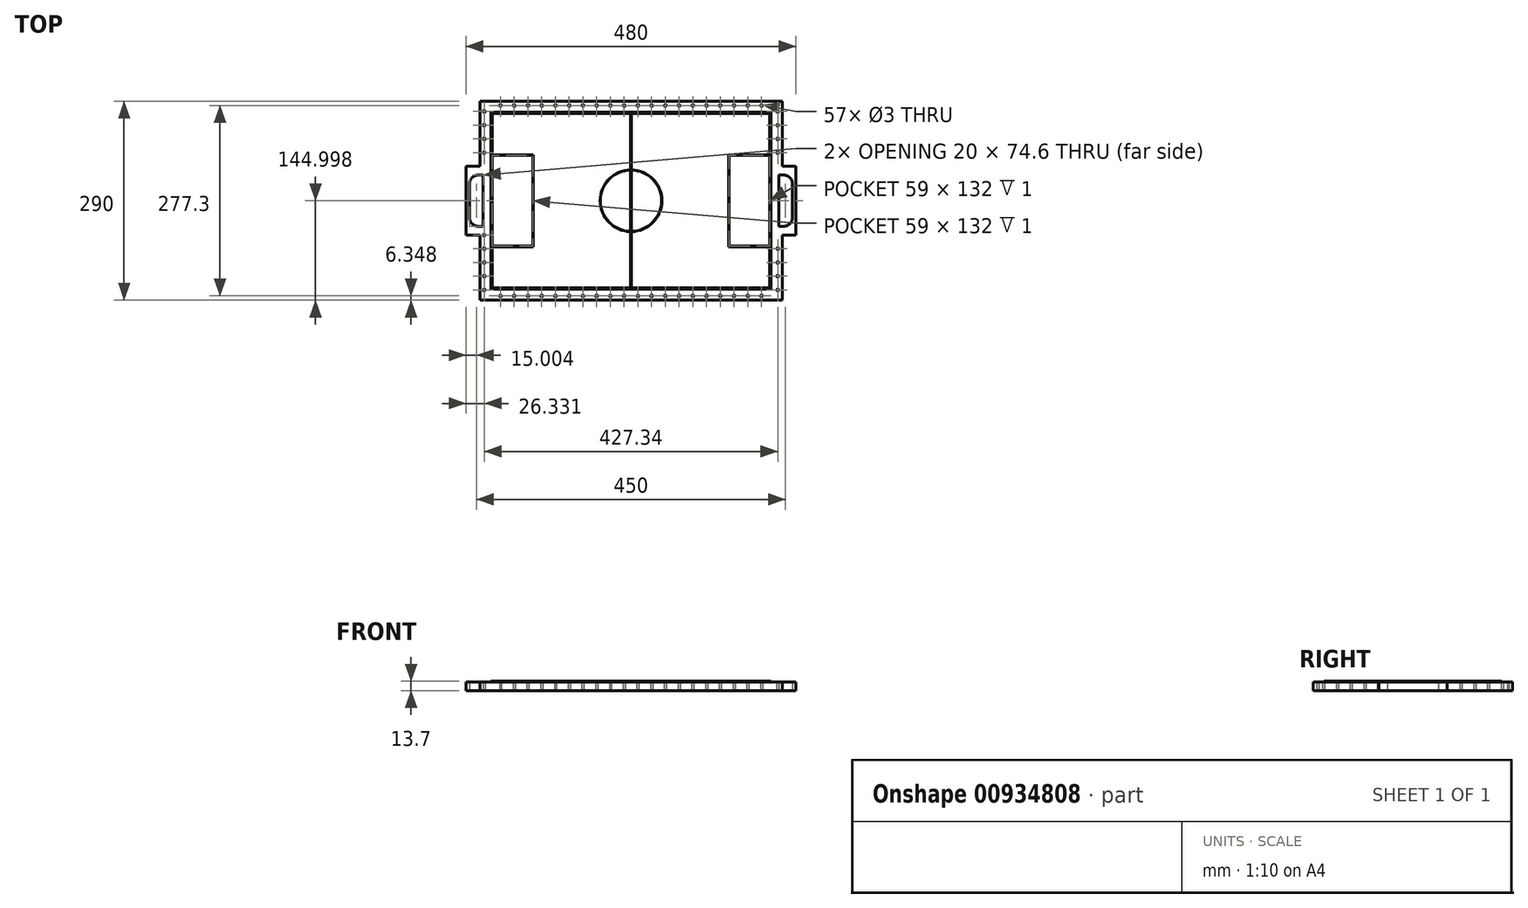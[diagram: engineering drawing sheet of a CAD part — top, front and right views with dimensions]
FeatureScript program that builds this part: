
annotation { "Feature Type Name" : "Feature", "Feature Type Description" : "" }
export const myFeature = defineFeature(function(context is Context, id is Id, definition is map)
    precondition{}
    {
        {
            var Q0;
            Q0=qCreatedBy(makeId("Top.planeOp"),FACE);
            var sketch = newSketch(context, id + "F0", { "sketchPlane" : qUnion([Q0])});
            skLineSegment(sketch, "E0.bottom", {"start": v(-336.05, 154.94) * mm, "end": v(103.95, 154.94) * mm});
            skLineSegment(sketch, "E0.top", {"start": v(-336.05, -135.06) * mm, "end": v(103.95, -135.06) * mm});
            skLineSegment(sketch, "E0.right", {"start": v(103.95, 154.94) * mm, "end": v(103.95, 59.94) * mm});
            skLineSegment(sketch, "E1", {"start": v(-116.05, -135.06) * mm, "end": v(-116.05, 154.94) * mm, "construction": true});
            skLineSegment(sketch, "E2", {"start": v(103.95, -40.06) * mm, "end": v(123.95, -40.06) * mm});
            skLineSegment(sketch, "E3", {"start": v(123.95, -40.06) * mm, "end": v(123.95, 59.94) * mm});
            skLineSegment(sketch, "E4", {"start": v(123.95, 59.94) * mm, "end": v(103.95, 59.94) * mm});
            skLineSegment(sketch, "E5.trimOffspring", {"start": v(103.95, -40.06) * mm, "end": v(103.95, -135.06) * mm});
            skLineSegment(sketch, "E6", {"start": v(-354.43, 9.94) * mm, "end": v(123.95, 9.94) * mm, "construction": true});
            skLineSegment(sketch, "E7.MirrorCS", {"start": v(-356.05, -40.06) * mm, "end": v(-356.05, 59.94) * mm});
            skLineSegment(sketch, "E8.MirrorCS", {"start": v(-336.05, -40.06) * mm, "end": v(-356.05, -40.06) * mm});
            skLineSegment(sketch, "E9.MirrorCS", {"start": v(-336.05, -40.06) * mm, "end": v(-336.05, -135.06) * mm});
            skLineSegment(sketch, "E10.MirrorCS", {"start": v(-336.05, 154.94) * mm, "end": v(-336.05, 59.94) * mm});
            skLineSegment(sketch, "E11.MirrorCS", {"start": v(-356.05, 59.94) * mm, "end": v(-336.05, 59.94) * mm});
            skLineSegment(sketch, "E12.bottom", {"start": v(98.95, -27.36) * mm, "end": v(106.25, -27.36) * mm});
            skLineSegment(sketch, "E12.top", {"start": v(98.95, 47.24) * mm, "end": v(106.25, 47.24) * mm});
            skLineSegment(sketch, "E12.left", {"start": v(98.95, -27.36) * mm, "end": v(98.95, 47.24) * mm});
            skLineSegment(sketch, "E12.right", {"start": v(118.95, -14.66) * mm, "end": v(118.95, 34.54) * mm});
            skPoint(sketch, "E13.visualSharp", {"position": v(118.95, -27.36) * mm});
            skArc(sketch, "E13.filletArc", {"start": v(106.25, -27.36) * mm, "mid": v(115.23, -23.64) * mm, "end": v(118.95, -14.66) * mm});
            skPoint(sketch, "E14.visualSharp", {"position": v(118.95, 47.24) * mm});
            skArc(sketch, "E14.filletArc", {"start": v(118.95, 34.54) * mm, "mid": v(115.23, 43.52) * mm, "end": v(106.25, 47.24) * mm});
            skLineSegment(sketch, "E15.MirrorCS", {"start": v(-331.05, -27.36) * mm, "end": v(-338.35, -27.36) * mm});
            skPoint(sketch, "E16.MirrorP", {"position": v(-351.05, 47.24) * mm});
            skLineSegment(sketch, "E17.MirrorCS", {"start": v(-331.05, 47.24) * mm, "end": v(-338.35, 47.24) * mm});
            skLineSegment(sketch, "E18.MirrorCS", {"start": v(-351.05, -14.66) * mm, "end": v(-351.05, 34.54) * mm});
            skPoint(sketch, "E19.MirrorP", {"position": v(-351.05, -27.36) * mm});
            skArc(sketch, "E20.MirrorCS", {"start": v(-351.05, 34.54) * mm, "mid": v(-347.33, 43.52) * mm, "end": v(-338.35, 47.24) * mm});
            skLineSegment(sketch, "E21.MirrorCS", {"start": v(-331.05, -27.36) * mm, "end": v(-331.05, 47.24) * mm});
            skArc(sketch, "E22.MirrorCS", {"start": v(-338.35, -27.36) * mm, "mid": v(-347.33, -23.64) * mm, "end": v(-351.05, -14.66) * mm});
            skLineSegment(sketch, "E23", {"start": v(-336.05, 148.59) * mm, "end": v(103.95, 148.59) * mm, "construction": true});
            skCircle(sketch, "E24", {"center": v(-306.05, 148.59) * mm, "radius": 1.5 * mm});
            skCircle(sketch, "E25.1.0.0", {"center": v(-286.05, 148.59) * mm, "radius": 1.5 * mm});
            skCircle(sketch, "E25.2.0.0", {"center": v(-266.05, 148.59) * mm, "radius": 1.5 * mm});
            skCircle(sketch, "E25.3.0.0", {"center": v(-246.05, 148.59) * mm, "radius": 1.5 * mm});
            skCircle(sketch, "E25.4.0.0", {"center": v(-226.05, 148.59) * mm, "radius": 1.5 * mm});
            skCircle(sketch, "E25.5.0.0", {"center": v(-206.05, 148.59) * mm, "radius": 1.5 * mm});
            skCircle(sketch, "E25.6.0.0", {"center": v(-186.05, 148.59) * mm, "radius": 1.5 * mm});
            skCircle(sketch, "E25.7.0.0", {"center": v(-166.05, 148.59) * mm, "radius": 1.5 * mm});
            skCircle(sketch, "E25.8.0.0", {"center": v(-146.05, 148.59) * mm, "radius": 1.5 * mm});
            skCircle(sketch, "E25.9.0.0", {"center": v(-126.05, 148.59) * mm, "radius": 1.5 * mm});
            skCircle(sketch, "E25.10.0.0", {"center": v(-106.05, 148.59) * mm, "radius": 1.5 * mm});
            skCircle(sketch, "E25.11.0.0", {"center": v(-86.05, 148.59) * mm, "radius": 1.5 * mm});
            skCircle(sketch, "E25.12.0.0", {"center": v(-66.05, 148.59) * mm, "radius": 1.5 * mm});
            skCircle(sketch, "E25.13.0.0", {"center": v(-46.05, 148.59) * mm, "radius": 1.5 * mm});
            skCircle(sketch, "E25.14.0.0", {"center": v(-26.05, 148.59) * mm, "radius": 1.5 * mm});
            skCircle(sketch, "E25.15.0.0", {"center": v(-6.05, 148.59) * mm, "radius": 1.5 * mm});
            skCircle(sketch, "E25.16.0.0", {"center": v(13.95, 148.59) * mm, "radius": 1.5 * mm});
            skCircle(sketch, "E25.17.0.0", {"center": v(33.95, 148.59) * mm, "radius": 1.5 * mm});
            skCircle(sketch, "E25.18.0.0", {"center": v(53.95, 148.59) * mm, "radius": 1.5 * mm});
            skCircle(sketch, "E25.19.0.0", {"center": v(73.95, 148.59) * mm, "radius": 1.5 * mm});
            skLineSegment(sketch, "E25.direction1", {"start": v(-306.05, 148.59) * mm, "end": v(-286.05, 148.59) * mm, "construction": true});
            skCircle(sketch, "E26.MirrorC", {"center": v(-306.05, -128.71) * mm, "radius": 1.5 * mm});
            skCircle(sketch, "E27.MirrorC", {"center": v(-286.05, -128.71) * mm, "radius": 1.5 * mm});
            skCircle(sketch, "E28.MirrorC", {"center": v(-246.05, -128.71) * mm, "radius": 1.5 * mm});
            skCircle(sketch, "E29.MirrorC", {"center": v(-26.05, -128.71) * mm, "radius": 1.5 * mm});
            skCircle(sketch, "E30.MirrorC", {"center": v(73.95, -128.71) * mm, "radius": 1.5 * mm});
            skCircle(sketch, "E31.MirrorC", {"center": v(53.95, -128.71) * mm, "radius": 1.5 * mm});
            skCircle(sketch, "E32.MirrorC", {"center": v(-6.05, -128.71) * mm, "radius": 1.5 * mm});
            skCircle(sketch, "E33.MirrorC", {"center": v(13.95, -128.71) * mm, "radius": 1.5 * mm});
            skCircle(sketch, "E34.MirrorC", {"center": v(-226.05, -128.71) * mm, "radius": 1.5 * mm});
            skCircle(sketch, "E35.MirrorC", {"center": v(-66.05, -128.71) * mm, "radius": 1.5 * mm});
            skCircle(sketch, "E36.MirrorC", {"center": v(-126.05, -128.71) * mm, "radius": 1.5 * mm});
            skCircle(sketch, "E37.MirrorC", {"center": v(-146.05, -128.71) * mm, "radius": 1.5 * mm});
            skCircle(sketch, "E38.MirrorC", {"center": v(-86.05, -128.71) * mm, "radius": 1.5 * mm});
            skCircle(sketch, "E39.MirrorC", {"center": v(-166.05, -128.71) * mm, "radius": 1.5 * mm});
            skCircle(sketch, "E40.MirrorC", {"center": v(33.95, -128.71) * mm, "radius": 1.5 * mm});
            skCircle(sketch, "E41.MirrorC", {"center": v(-46.05, -128.71) * mm, "radius": 1.5 * mm});
            skCircle(sketch, "E42.MirrorC", {"center": v(-266.05, -128.71) * mm, "radius": 1.5 * mm});
            skCircle(sketch, "E43.MirrorC", {"center": v(-206.05, -128.71) * mm, "radius": 1.5 * mm});
            skCircle(sketch, "E44.MirrorC", {"center": v(-186.05, -128.71) * mm, "radius": 1.5 * mm});
            skCircle(sketch, "E45.MirrorC", {"center": v(-106.05, -128.71) * mm, "radius": 1.5 * mm});
            skLineSegment(sketch, "E46.MirrorCS", {"start": v(-306.05, -128.71) * mm, "end": v(-286.05, -128.71) * mm, "construction": true});
            skLineSegment(sketch, "E47", {"start": v(-329.7, 154.94) * mm, "end": v(-329.7, -135.06) * mm, "construction": true});
            skCircle(sketch, "E48", {"center": v(-329.7, 139.94) * mm, "radius": 1.5 * mm});
            skCircle(sketch, "E49.1.0.0", {"center": v(-329.7, 119.94) * mm, "radius": 1.5 * mm});
            skCircle(sketch, "E49.2.0.0", {"center": v(-329.7, 99.94) * mm, "radius": 1.5 * mm});
            skCircle(sketch, "E49.3.0.0", {"center": v(-329.71, 79.94) * mm, "radius": 1.5 * mm});
            skLineSegment(sketch, "E49.direction1", {"start": v(-329.7, 139.94) * mm, "end": v(-329.7, 119.94) * mm, "construction": true});
            skCircle(sketch, "E50.MirrorC", {"center": v(-329.71, -60.06) * mm, "radius": 1.5 * mm});
            skLineSegment(sketch, "E51.MirrorCS", {"start": v(-329.7, -120.06) * mm, "end": v(-329.7, -100.06) * mm, "construction": true});
            skCircle(sketch, "E52.MirrorC", {"center": v(-329.7, -120.06) * mm, "radius": 1.5 * mm});
            skCircle(sketch, "E53.MirrorC", {"center": v(-329.7, -100.06) * mm, "radius": 1.5 * mm});
            skCircle(sketch, "E54.MirrorC", {"center": v(-329.7, -80.06) * mm, "radius": 1.5 * mm});
            skCircle(sketch, "E55.MirrorC", {"center": v(-329.72, -40.06) * mm, "radius": 1.5 * mm});
            skCircle(sketch, "E56.MirrorC", {"center": v(97.62, -60.06) * mm, "radius": 1.5 * mm});
            skCircle(sketch, "E57.MirrorC", {"center": v(97.62, -80.06) * mm, "radius": 1.5 * mm});
            skCircle(sketch, "E58.MirrorC", {"center": v(97.6, -120.06) * mm, "radius": 1.5 * mm});
            skCircle(sketch, "E59.MirrorC", {"center": v(97.6, -100.06) * mm, "radius": 1.5 * mm});
            skLineSegment(sketch, "E60.MirrorCS", {"start": v(97.6, -120.06) * mm, "end": v(97.6, -100.06) * mm, "construction": true});
            skCircle(sketch, "E61.MirrorC", {"center": v(97.6, 139.94) * mm, "radius": 1.5 * mm});
            skCircle(sketch, "E62.MirrorC", {"center": v(97.62, 99.94) * mm, "radius": 1.5 * mm});
            skLineSegment(sketch, "E63.MirrorCS", {"start": v(97.6, 139.94) * mm, "end": v(97.6, 119.94) * mm, "construction": true});
            skCircle(sketch, "E64.MirrorC", {"center": v(97.6, 119.94) * mm, "radius": 1.5 * mm});
            skCircle(sketch, "E65.MirrorC", {"center": v(97.62, 79.94) * mm, "radius": 1.5 * mm});
            skSolve(sketch);
        }
        {
            var Q0;
            Q0 = qSketchRegion(id + "F0", true);
            extrude(context, id + "F1", {"entities" : qUnion([Q0]), "depth" : 12.7 * mm, "offsetDistance" : 25 * mm});
        }
        {
            var Q0;
            Q0=makeQuery(id+"F1.opExtrude","CAP_FACE",FACE,{"disambiguationData":[OSD([sQuery(id+"F0.wireOp",EDGE,"E0.bottom"),sQuery(id+"F0.wireOp",EDGE,"E0.top"),sQuery(id+"F0.wireOp",EDGE,"E0.right"),sQuery(id+"F0.wireOp",EDGE,"E2"),sQuery(id+"F0.wireOp",EDGE,"E3"),sQuery(id+"F0.wireOp",EDGE,"E4"),sQuery(id+"F0.wireOp",EDGE,"E5.trimOffspring"),sQuery(id+"F0.wireOp",EDGE,"E7.MirrorCS"),sQuery(id+"F0.wireOp",EDGE,"E8.MirrorCS"),sQuery(id+"F0.wireOp",EDGE,"E9.MirrorCS"),sQuery(id+"F0.wireOp",EDGE,"E10.MirrorCS"),sQuery(id+"F0.wireOp",EDGE,"E11.MirrorCS"),sQuery(id+"F0.wireOp",EDGE,"E12.bottom"),sQuery(id+"F0.wireOp",EDGE,"E12.top"),sQuery(id+"F0.wireOp",EDGE,"E12.left"),sQuery(id+"F0.wireOp",EDGE,"E12.right"),sQuery(id+"F0.wireOp",EDGE,"E13.filletArc"),sQuery(id+"F0.wireOp",EDGE,"E14.filletArc"),sQuery(id+"F0.wireOp",EDGE,"E15.MirrorCS"),sQuery(id+"F0.wireOp",EDGE,"E17.MirrorCS"),sQuery(id+"F0.wireOp",EDGE,"E18.MirrorCS"),sQuery(id+"F0.wireOp",EDGE,"E20.MirrorCS"),sQuery(id+"F0.wireOp",EDGE,"E21.MirrorCS"),sQuery(id+"F0.wireOp",EDGE,"E22.MirrorCS")])],"isStart":false});
            var sketch = newSketch(context, id + "F2", { "sketchPlane" : qUnion([Q0])});
            skLineSegment(sketch, "E66.bottom", {"start": v(-320.05, 138.94) * mm, "end": v(87.95, 138.94) * mm});
            skLineSegment(sketch, "E66.top", {"start": v(-320.05, -119.06) * mm, "end": v(87.95, -119.06) * mm});
            skLineSegment(sketch, "E66.left", {"start": v(-320.05, 138.94) * mm, "end": v(-320.05, -119.06) * mm});
            skLineSegment(sketch, "E66.right", {"start": v(87.95, 138.94) * mm, "end": v(87.95, -119.06) * mm});
            skLineSegment(sketch, "E67.0", {"start": v(-318.05, 136.94) * mm, "end": v(-116.55, 136.94) * mm});
            skLineSegment(sketch, "E67.1", {"start": v(-318.05, 136.94) * mm, "end": v(-318.05, 76.94) * mm});
            skLineSegment(sketch, "E67.2", {"start": v(-318.05, -117.06) * mm, "end": v(-116.55, -117.06) * mm});
            skLineSegment(sketch, "E67.3", {"start": v(85.95, 136.94) * mm, "end": v(85.95, 76.94) * mm});
            skLineSegment(sketch, "E68", {"start": v(-116.05, 136.94) * mm, "end": v(-116.05, -117.06) * mm, "construction": true});
            skLineSegment(sketch, "E69", {"start": v(-115.55, 136.94) * mm, "end": v(-115.55, 54.94) * mm});
            skLineSegment(sketch, "E70.MirrorCS", {"start": v(-116.55, 136.94) * mm, "end": v(-116.55, 54.94) * mm});
            skLineSegment(sketch, "E71.trimOffspring", {"start": v(-115.55, 136.94) * mm, "end": v(85.95, 136.94) * mm});
            skLineSegment(sketch, "E72.trimOffspring", {"start": v(-115.55, -117.06) * mm, "end": v(85.95, -117.06) * mm});
            skLineSegment(sketch, "E73", {"start": v(-318.05, 9.94) * mm, "end": v(85.95, 9.94) * mm, "construction": true});
            skArc(sketch, "E74", {"start": v(-116.55, 54.94) * mm, "mid": v(-161.05, 9.94) * mm, "end": v(-116.55, -35.06) * mm});
            skArc(sketch, "E75", {"start": v(-116.55, 54.44) * mm, "mid": v(-160.55, 9.94) * mm, "end": v(-116.55, -34.56) * mm});
            skLineSegment(sketch, "E76", {"start": v(-318.05, -57.06) * mm, "end": v(-258.05, -57.06) * mm});
            skLineSegment(sketch, "E77", {"start": v(-258.05, -57.06) * mm, "end": v(-258.05, 76.94) * mm});
            skLineSegment(sketch, "E78", {"start": v(-258.05, 76.94) * mm, "end": v(-318.05, 76.94) * mm});
            skLineSegment(sketch, "E79.0", {"start": v(-259.05, 75.94) * mm, "end": v(-318.05, 75.94) * mm});
            skLineSegment(sketch, "E79.1", {"start": v(-259.05, -56.06) * mm, "end": v(-259.05, 75.94) * mm});
            skLineSegment(sketch, "E79.2", {"start": v(-318.05, -56.06) * mm, "end": v(-259.05, -56.06) * mm});
            skLineSegment(sketch, "E80.MirrorCS", {"start": v(25.95, -57.06) * mm, "end": v(25.95, 76.94) * mm});
            skLineSegment(sketch, "E81.MirrorCS", {"start": v(26.95, 75.94) * mm, "end": v(85.95, 75.94) * mm});
            skLineSegment(sketch, "E82.MirrorCS", {"start": v(85.95, -56.06) * mm, "end": v(26.95, -56.06) * mm});
            skLineSegment(sketch, "E83.MirrorCS", {"start": v(26.95, -56.06) * mm, "end": v(26.95, 75.94) * mm});
            skLineSegment(sketch, "E84.MirrorCS", {"start": v(85.95, -57.06) * mm, "end": v(25.95, -57.06) * mm});
            skLineSegment(sketch, "E85.MirrorCS", {"start": v(25.95, 76.94) * mm, "end": v(85.95, 76.94) * mm});
            skLineSegment(sketch, "E86.trimOffspring", {"start": v(-318.05, 75.94) * mm, "end": v(-318.05, -56.06) * mm});
            skLineSegment(sketch, "E87.trimOffspring", {"start": v(-318.05, -57.06) * mm, "end": v(-318.05, -117.06) * mm});
            skLineSegment(sketch, "E88.trimOffspring", {"start": v(-115.55, 54.44) * mm, "end": v(-115.55, -34.56) * mm});
            skLineSegment(sketch, "E89.trimOffspring", {"start": v(-116.55, 54.44) * mm, "end": v(-116.55, -34.56) * mm});
            skArc(sketch, "E90.trimOffspring", {"start": v(-115.55, -34.56) * mm, "mid": v(-71.55, 9.94) * mm, "end": v(-115.55, 54.44) * mm});
            skLineSegment(sketch, "E91.trimOffspring", {"start": v(-115.55, -35.06) * mm, "end": v(-115.55, -117.06) * mm});
            skArc(sketch, "E92.trimOffspring", {"start": v(-115.55, -35.06) * mm, "mid": v(-71.05, 9.94) * mm, "end": v(-115.55, 54.94) * mm});
            skLineSegment(sketch, "E93.trimOffspring", {"start": v(-116.55, -35.06) * mm, "end": v(-116.55, -117.06) * mm});
            skLineSegment(sketch, "E94.trimOffspring", {"start": v(85.95, 75.94) * mm, "end": v(85.95, -56.06) * mm});
            skLineSegment(sketch, "E95.trimOffspring", {"start": v(85.95, -57.06) * mm, "end": v(85.95, -117.06) * mm});
            skSolve(sketch);
        }
        {
            var Q0;
            Q0 = qSketchRegion(id + "F2", true);
            extrude(context, id + "F3", {"entities" : qUnion([Q0]), "operationType" : NewBodyOperationType.ADD, "depth" : 1 * mm, "offsetDistance" : 25 * mm});
        }
    });
